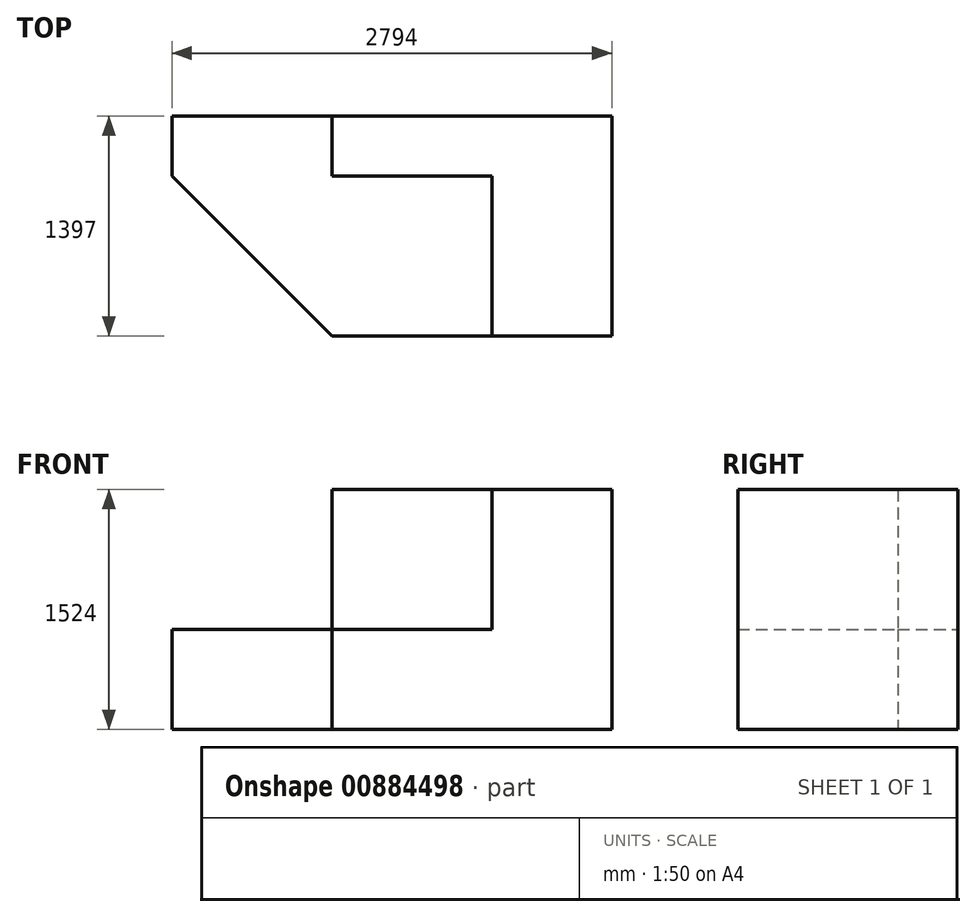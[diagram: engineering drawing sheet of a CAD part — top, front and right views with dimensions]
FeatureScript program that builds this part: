
annotation { "Feature Type Name" : "Feature", "Feature Type Description" : "" }
export const myFeature = defineFeature(function(context is Context, id is Id, definition is map)
    precondition{}
    {
        {
            var Q0;
            Q0=qCreatedBy(makeId("Top.planeOp"),FACE);
            var sketch = newSketch(context, id + "F0", { "sketchPlane" : qUnion([Q0])});
            skLineSegment(sketch, "E0.bottom", {"start": v(0, 0) * mm, "end": v(-1778, 0) * mm});
            skLineSegment(sketch, "E0.top", {"start": v(0, 1397) * mm, "end": v(-1778, 1397) * mm});
            skLineSegment(sketch, "E0.left", {"start": v(0, 0) * mm, "end": v(0, 1397) * mm});
            skLineSegment(sketch, "E0.right", {"start": v(-1778, 0) * mm, "end": v(-1778, 1397) * mm});
            skSolve(sketch);
        }
        {
            var Q0;
            Q0=makeQuery(id+"F0.imprint","IMPRINT",FACE,{"disambiguationData":[TD([[makeQuery(id+"F0.imprint","IMPRINT",EDGE,{"derivedFrom":sQuery(id+"F0.wireOp",EDGE,"E0.bottom")}),-1.0]])]});
            extrude(context, id + "F1", {"entities" : qUnion([Q0]), "depth" : 635 * mm, "offsetDistance" : 25.4 * mm});
        }
        {
            var Q0;
            Q0=makeQuery(id+"F1.opExtrude","CAP_FACE",FACE,{"disambiguationData":[OSD([sQuery(id+"F0.wireOp",EDGE,"E0.bottom"),sQuery(id+"F0.wireOp",EDGE,"E0.top"),sQuery(id+"F0.wireOp",EDGE,"E0.left"),sQuery(id+"F0.wireOp",EDGE,"E0.right")])],"isStart":false});
            var sketch = newSketch(context, id + "F2", { "sketchPlane" : qUnion([Q0])});
            skLineSegment(sketch, "E1.bottom", {"start": v(0, 0) * mm, "end": v(-762, 0) * mm});
            skLineSegment(sketch, "E1.top", {"start": v(0, 1016) * mm, "end": v(-762, 1016) * mm});
            skLineSegment(sketch, "E1.left", {"start": v(0, 0) * mm, "end": v(0, 1016) * mm});
            skLineSegment(sketch, "E1.right", {"start": v(-762, 0) * mm, "end": v(-762, 1016) * mm});
            skSolve(sketch);
        }
        {
            var Q0;
            Q0=makeQuery(id+"F2.imprint","IMPRINT",FACE,{"disambiguationData":[TD([[makeQuery(id+"F2.imprint","IMPRINT",EDGE,{"derivedFrom":sQuery(id+"F2.wireOp",EDGE,"E1.bottom")}),-1.0]])]});
            extrude(context, id + "F3", {"entities" : qUnion([Q0]), "operationType" : NewBodyOperationType.ADD, "depth" : 1143 * mm, "offsetDistance" : 25.4 * mm});
        }
        {
            var Q0;
            Q0=makeQuery(id+"F1.opExtrude","CAP_FACE",FACE,{"disambiguationData":[OSD([sQuery(id+"F0.wireOp",EDGE,"E0.bottom"),sQuery(id+"F0.wireOp",EDGE,"E0.top"),sQuery(id+"F0.wireOp",EDGE,"E0.left"),sQuery(id+"F0.wireOp",EDGE,"E0.right")])],"isStart":false});
            var sketch = newSketch(context, id + "F4", { "sketchPlane" : qUnion([Q0])});
            skLineSegment(sketch, "E2.bottom", {"start": v(0, 1397) * mm, "end": v(-1778, 1397) * mm});
            skLineSegment(sketch, "E2.top", {"start": v(0, 1016) * mm, "end": v(-1778, 1016) * mm});
            skLineSegment(sketch, "E2.left", {"start": v(0, 1397) * mm, "end": v(0, 1016) * mm});
            skLineSegment(sketch, "E2.right", {"start": v(-1778, 1397) * mm, "end": v(-1778, 1016) * mm});
            skSolve(sketch);
        }
        {
            var Q0;
            Q0=makeQuery(id+"F4.imprint","IMPRINT",FACE,{"disambiguationData":[TD([[makeQuery(id+"F4.imprint","IMPRINT",EDGE,{"derivedFrom":sQuery(id+"F4.wireOp",EDGE,"E2.bottom")}),1.0]])]});
            extrude(context, id + "F5", {"entities" : qUnion([Q0]), "operationType" : NewBodyOperationType.ADD, "depth" : 889 * mm, "offsetDistance" : 25.4 * mm});
        }
        {
            var Q0;
            Q0=makeQuery(id+"F3.opExtrude","CAP_FACE",FACE,{"disambiguationData":[OSD([sQuery(id+"F2.wireOp",EDGE,"E1.bottom"),sQuery(id+"F2.wireOp",EDGE,"E1.top"),sQuery(id+"F2.wireOp",EDGE,"E1.left"),sQuery(id+"F2.wireOp",EDGE,"E1.right")])],"isStart":false});
            extrude(context, id + "F6", {"entities" : qUnion([Q0]), "operationType" : NewBodyOperationType.REMOVE, "oppositeDirection" : true, "depth" : 254 * mm, "offsetDistance" : 25.4 * mm});
        }
        {
            var Q0;
            Q0=makeQuery(id+"F1.opExtrude","CAP_FACE",FACE,{"disambiguationData":[OSD([sQuery(id+"F0.wireOp",EDGE,"E0.bottom"),sQuery(id+"F0.wireOp",EDGE,"E0.top"),sQuery(id+"F0.wireOp",EDGE,"E0.left"),sQuery(id+"F0.wireOp",EDGE,"E0.right")])],"isStart":true});
            var sketch = newSketch(context, id + "F7", { "sketchPlane" : qUnion([Q0])});
            skLineSegment(sketch, "E3", {"start": v(-1778, -1397) * mm, "end": v(-2794, -1397) * mm});
            skLineSegment(sketch, "E4", {"start": v(-2794, -1397) * mm, "end": v(-2794, -1016) * mm});
            skLineSegment(sketch, "E5", {"start": v(-2794, -1016) * mm, "end": v(-1778, 0) * mm});
            skSolve(sketch);
        }
        {
            var Q0;
            Q0=makeQuery(id+"F7.imprint","IMPRINT",FACE,{"disambiguationData":[TD([[makeQuery(id+"F7.imprint","IMPRINT",EDGE,{"derivedFrom":sQuery(id+"F7.wireOp",EDGE,"E3")}),-1.0]])]});
            extrude(context, id + "F8", {"entities" : qUnion([Q0]), "operationType" : NewBodyOperationType.ADD, "oppositeDirection" : true, "depth" : 635 * mm, "offsetDistance" : 25.4 * mm});
        }
    });
